# Revit family: Bicomics_dimshtora_EI60
name_source: partatom
category: Обобщенные модели
revit_build: Autodesk Revit 2016 (Build: 20150714_1515(x64)
units: mm (PartAtom-declared; Revit-internal decimal feet)

## family parameters
Всегда вертикально = Да
Может служить основой для арматурных стержней = Нет
Общий = Нет
Основа = Стена
При загрузке вырезать с полостями = Нет
Размер круглого соединителя = Использовать диаметр
Тип детали = Нормальный
Точка расчета площади = Нет

## types (2) — shared parameters
ADSK_Единица измерения = шт.
URL = http://fireproof.bikoms.ru
Видимость 1 = Да
Видимость 2 = Нет
Видимость 3 = Да
Видимость 4 = Нет
Видимость 5 = Нет
Высота люка = 300 мм
Выступ = 1 мм
Глубина направляющих = 45 мм
Движение коннектора по x = 10 мм
Движение планки по x = 19 мм
Движение по y = 500 мм
Изготовитель = Бикомикс
Ключевая пометка = ﻿﻿ ​ ​​​​​​   ﻿ ​   ﻿       ​ ﻿ ​ ​ ﻿ ​   ﻿       ​ ﻿   ﻿     ﻿   ​       ﻿  ﻿ ﻿   ﻿ ﻿   ﻿        ​​ ​        ​ ﻿   ​ ﻿ ​                ﻿                ​  ﻿        ﻿﻿
Код по классификатору = ﻿﻿ ​ ​​​​​​   ﻿ ​   ﻿       ​ ﻿ ​ ​ ﻿ ​   ﻿       ​ ﻿   ﻿     ﻿   ​       ﻿  ﻿ ﻿   ﻿ ﻿   ﻿        ​​ ​        ​ ﻿   ​ ﻿ ​                ﻿                ​  ﻿        ﻿﻿
Комментарии к типоразмеру = ﻿﻿ ​ ​​​​​​   ﻿ ​   ﻿       ​ ﻿ ​ ​ ﻿ ​   ﻿       ​ ﻿   ﻿     ﻿   ​       ﻿  ﻿ ﻿   ﻿ ﻿   ﻿        ​​ ​        ​ ﻿   ​ ﻿ ​                ﻿                ​  ﻿        ﻿﻿
Материал короба = Сталь х/к 0,8ПС  1.5мм
Материал направляющих = Сталь х/к 0,8ПС  1.5мм
Направляющие в проем слева = Нет
Направляющие в проем справа = Нет
Описание = ﻿﻿ ​ ​​​​​​   ﻿ ​   ﻿       ​ ﻿ ​ ​ ﻿ ​   ﻿       ​ ﻿   ﻿     ﻿   ​       ﻿  ﻿ ﻿   ﻿ ﻿   ﻿        ​​ ​        ​ ﻿   ​ ﻿ ​                ﻿                ​  ﻿        ﻿﻿
Снаружи слева = Да
Снаружи справа = Да
Ток = 10 А
Толщина направляющих = 90 мм
Толщина полотна = 15 мм
Ширина лаза = 50 мм
Ширина люка = 150 мм
Штора открыто = Нет
Электросеть = 220 В
расположение люка = 1000 мм

## per-type parameters (varying)
| type | FL_Таблица1 | Материал полотна |
| Дымозащитная штора ШДЗ E 120 | СеткаКоробов120 | Полотно EI 120 |
| Дымозащитная штора ШДЗ E 30 | СеткаКоробов30 | Полотно EI 30 |

## geometry (parser evidence)
native form markers: Blend x2
no freeform markers — native parametric forms only
